# Revit family: ControlHoist_Optima_Raynor
name_source: partatom
category: Electrical Fixtures
units: mm (PartAtom-declared; Revit-internal decimal feet)

## family parameters
Always vertical = No
Classification Number = 23.30.40.11.34
Cut with Voids When Loaded = No
Maintain Annotation Orientation = No
Part Type = Normal
Room Calculation Point = No
Round Connector Dimension = Use Diameter
Shared = No
Work Plane-Based = Yes

## types (1)
- ByType
    Assembly Code = B2030410
    Chain Material = Galvanized Steel
    Construction Details = http://www.raynor.com
    Default Elevation = 0"
    Depth = 15"
    Description = Door Control as Specified in 08 36 00
    Expected Lifespan (Years) = 0
    Height = 30"
    Horsepower = 0.00 hp
    Housing Material = Galvanized Steel, Powder Coated Black
    Installation_Fabricaton = http://www.raynor.com
    Jackshaft Mount = Yes
    Keynote = 08330
    Maintenance Schedule (Months) = 0
    Manufacturer = Raynor
    Manufacturer Fax = 888-598-4790
    Manufacturer Website = http://www.raynor.com
    Model = As Specified in 08 36 00
    Number of Poles = 1
    Phase = 1
    Power Factor = 1
    Product Data = http://www.arcat.com
    Product Properties = http://www.arcat.com
    Radius = 3 1/4"
    Revision = R1_1-2010
    Sales Information = http://www.raynor.com
    Send Message = http://www.arcat.com
    Specification = http://www.arcat.com
    Trolley Mount = No
    URL = http://www.raynor.com
    Voltage = 0 V
    Warranty Duration (Years) = 0
    Width = 9 1/2"
    asdf = 4"

## geometry (parser evidence)
native form markers: Blend x6, Sweep x4
no freeform markers — native parametric forms only
